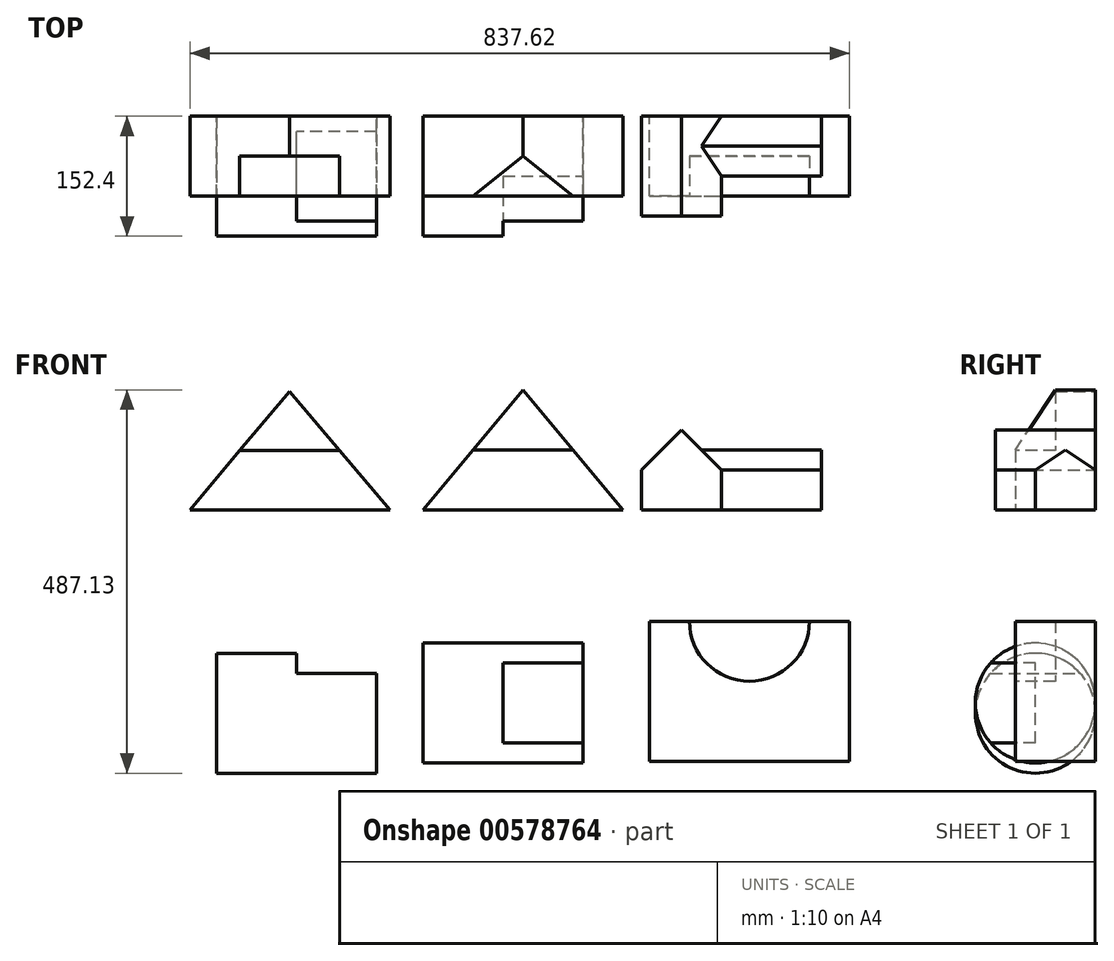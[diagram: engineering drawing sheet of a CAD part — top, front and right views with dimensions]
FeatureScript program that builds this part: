
annotation { "Feature Type Name" : "Feature", "Feature Type Description" : "" }
export const myFeature = defineFeature(function(context is Context, id is Id, definition is map)
    precondition{}
    {
        {
            var Q0;
            Q0=qCreatedBy(makeId("Front.planeOp"),FACE);
            var sketch = newSketch(context, id + "F0", { "sketchPlane" : qUnion([Q0])});
            skLineSegment(sketch, "E0", {"start": v(0, 0) * mm, "end": v(-254, 0) * mm});
            skLineSegment(sketch, "E1", {"start": v(-254, 0) * mm, "end": v(-127, 0) * mm});
            skLineSegment(sketch, "E2", {"start": v(-127.85, 149.9) * mm, "end": v(-254, 0) * mm});
            skLineSegment(sketch, "E3", {"start": v(-127.85, 149.9) * mm, "end": v(0, 0) * mm});
            skLineSegment(sketch, "E4", {"start": v(-127, 76.2) * mm, "end": v(-190.92, 76.2) * mm});
            skPoint(sketch, "E4.endSnap0", {"position": v(-190.92, 74.95) * mm});
            skLineSegment(sketch, "E5", {"start": v(-127, 76.2) * mm, "end": v(-65, 76.2) * mm});
            skLineSegment(sketch, "E6", {"start": v(-127, 0) * mm, "end": v(-127, 76.2) * mm});
            skSolve(sketch);
        }
        {
            var Q0;
            {var subQ0=sQuery(id+"F0.wireOp",EDGE,"E1");Q0=makeQuery(id+"F0.imprint","IMPRINT",FACE,{"disambiguationData":[TD([[makeQuery(id+"F0.imprint","IMPRINT",EDGE,{"derivedFrom":subQ0}),1.0]])]});}
            var Q1;
            {var subQ0=sQuery(id+"F0.wireOp",EDGE,"E0");Q1=makeQuery(id+"F0.imprint","IMPRINT",FACE,{"disambiguationData":[TD([[makeQuery(id+"F0.imprint","IMPRINT",EDGE,{"derivedFrom":subQ0}),-1.0]])]});}
            var Q2;
            {var subQ5=sQuery(id+"F0.wireOp",EDGE,"E5");Q2=makeQuery(id+"F0.imprint","IMPRINT",FACE,{"disambiguationData":[TD([[makeQuery(id+"F0.imprint","IMPRINT",EDGE,{"derivedFrom":subQ5}),1.0]])]});}
            extrude(context, id + "F1", {"entities" : qUnion([Q0, Q1, Q2]), "depth" : 101.6 * mm, "offsetDistance" : 25.4 * mm});
        }
        {
            var Q0;
            Q0=makeQuery(id+"F1.opExtrude","CAP_FACE",FACE,{"disambiguationData":[OSD([sQuery(id+"F0.wireOp",EDGE,"E0"),sQuery(id+"F0.wireOp",EDGE,"E1"),sQuery(id+"F0.wireOp",EDGE,"E2"),sQuery(id+"F0.wireOp",EDGE,"E3")])],"isStart":false});
            var sketch = newSketch(context, id + "F2", { "sketchPlane" : qUnion([Q0])});
            skLineSegment(sketch, "E7", {"start": v(-127, 74.95) * mm, "end": v(-63.92, 74.95) * mm});
            skPoint(sketch, "E7.startSnap0", {"position": v(-127, 0) * mm});
            skPoint(sketch, "E7.startSnap1", {"position": v(-127.85, 74.95) * mm});
            skLineSegment(sketch, "E8", {"start": v(-127, 74.95) * mm, "end": v(-190.92, 74.95) * mm});
            skSolve(sketch);
        }
        {
            var Q0;
            {var subQ0=sQuery(id+"F2.wireOp",EDGE,"E7");Q0=makeQuery(id+"F2.imprint","IMPRINT",FACE,{"disambiguationData":[TD([[makeQuery(id+"F2.imprint","IMPRINT",EDGE,{"derivedFrom":subQ0}),1.0]])]});}
            extrude(context, id + "F3", {"entities" : qUnion([Q0]), "operationType" : NewBodyOperationType.REMOVE, "oppositeDirection" : true, "depth" : 50.8 * mm, "offsetDistance" : 25.4 * mm});
        }
        {
            var Q0;
            Q0=qCreatedBy(makeId("Front.planeOp"),FACE);
            var sketch = newSketch(context, id + "F4", { "sketchPlane" : qUnion([Q0])});
            skLineSegment(sketch, "E9", {"start": v(42.1, 0) * mm, "end": v(296.1, 0) * mm});
            skLineSegment(sketch, "E10", {"start": v(169.1, 152.4) * mm, "end": v(42.1, 0) * mm});
            skLineSegment(sketch, "E11", {"start": v(169.1, 152.4) * mm, "end": v(296.1, 0) * mm});
            skLineSegment(sketch, "E12", {"start": v(169.1, 76.2) * mm, "end": v(105.6, 76.2) * mm});
            skLineSegment(sketch, "E13", {"start": v(169.1, 76.2) * mm, "end": v(232.6, 76.2) * mm});
            skSolve(sketch);
        }
        {
            var Q0;
            {var subQ1=sQuery(id+"F4.wireOp",EDGE,"E9");Q0=makeQuery(id+"F4.imprint","IMPRINT",FACE,{"disambiguationData":[TD([[makeQuery(id+"F4.imprint","IMPRINT",EDGE,{"derivedFrom":subQ1}),1.0]])]});}
            var Q1;
            {var subQ3=sQuery(id+"F4.wireOp",EDGE,"E12");Q1=makeQuery(id+"F4.imprint","IMPRINT",FACE,{"disambiguationData":[TD([[makeQuery(id+"F4.imprint","IMPRINT",EDGE,{"derivedFrom":subQ3}),-1.0]])]});}
            extrude(context, id + "F5", {"entities" : qUnion([Q0, Q1]), "depth" : 101.6 * mm, "offsetDistance" : 25.4 * mm});
        }
        {
            var Q0;
            Q0=makeQuery(id+"F5.opExtrude","CAP_EDGE",EDGE,{"disambiguationData":[OSD([sQuery(id+"F4.wireOp",EDGE,"E9")])],"isStart":false});
            cPoint(context, id + "F6", {"entities" : qUnion([Q0]), "parameter" : 0.5});
        }
        {
            var Q0;
            Q0=makeQuery(id+"F5.opExtrude","CAP_VERTEX",VERTEX,{"disambiguationData":[OSD([sQuery(id+"F4.wireOp",EDGE,"E10"),sQuery(id+"F4.wireOp",EDGE,"E11")])],"isStart":true});
            var Q1;
            Q1=makeQuery(id+"F5.opExtrude","CAP_VERTEX",VERTEX,{"disambiguationData":[OSD([sQuery(id+"F4.wireOp",EDGE,"E10"),sQuery(id+"F4.wireOp",EDGE,"E11")])],"isStart":false});
            var Q2;
            Q2 = qCreatedBy(id + "F6" ,VERTEX);
            cPlane(context, id + "F7", {"entities" : qUnion([Q0, Q1, Q2]), "cplaneType" : CPlaneType.THREE_POINT, "offset" : 25.4 * mm, "width" : 152.4 * mm, "height" : 152.4 * mm});
        }
        {
            var Q0;
            Q0=qCreatedBy(id+"F7.planeOp",FACE);
            var sketch = newSketch(context, id + "F8", { "sketchPlane" : qUnion([Q0])});
            skLineSegment(sketch, "E14", {"start": v(101.6, 76.2) * mm, "end": v(50.8, 152.4) * mm});
            skLineSegment(sketch, "E15", {"start": v(50.8, 152.4) * mm, "end": v(101.6, 152.4) * mm});
            skLineSegment(sketch, "E16", {"start": v(101.6, 152.4) * mm, "end": v(101.6, 76.2) * mm});
            skSolve(sketch);
        }
        {
            var Q0;
            Q0 = qSketchRegion(id + "F8", true);
            extrude(context, id + "F9", {"entities" : qUnion([Q0]), "operationType" : NewBodyOperationType.REMOVE, "endBound" : BoundingType.SYMMETRIC, "depth" : 157.48 * mm, "offsetDistance" : 25.4 * mm});
        }
        {
            var Q0;
            Q0=qCreatedBy(makeId("Front.planeOp"),FACE);
            var sketch = newSketch(context, id + "F10", { "sketchPlane" : qUnion([Q0])});
            skLineSegment(sketch, "E17.bottom", {"start": v(319.7, 0) * mm, "end": v(421.3, 0) * mm});
            skLineSegment(sketch, "E18", {"start": v(370.5, 101.6) * mm, "end": v(319.7, 50.8) * mm});
            skLineSegment(sketch, "E19", {"start": v(370.5, 101.6) * mm, "end": v(421.3, 50.8) * mm});
            skLineSegment(sketch, "E20", {"start": v(319.7, 50.8) * mm, "end": v(319.7, 0) * mm});
            skLineSegment(sketch, "E21", {"start": v(421.3, 0) * mm, "end": v(421.3, 50.8) * mm});
            skSolve(sketch);
        }
        {
            var Q0;
            Q0=makeQuery(id+"F10.imprint","IMPRINT",FACE,{"disambiguationData":[TD([[makeQuery(id+"F10.imprint","IMPRINT",EDGE,{"derivedFrom":sQuery(id+"F10.wireOp",EDGE,"E17.bottom")}),1.0]])]});
            extrude(context, id + "F11", {"entities" : qUnion([Q0]), "depth" : 127 * mm, "offsetDistance" : 25.4 * mm});
        }
        {
            var Q0;
            Q0=makeQuery(id+"F11.opExtrude","CAP_EDGE",EDGE,{"disambiguationData":[OSD([sQuery(id+"F10.wireOp",EDGE,"E17.bottom")])],"isStart":false});
            cPoint(context, id + "F12", {"entities" : qUnion([Q0]), "parameter" : 0.5});
        }
        {
            var Q0;
            Q0=makeQuery(id+"F11.opExtrude","CAP_VERTEX",VERTEX,{"disambiguationData":[OSD([sQuery(id+"F10.wireOp",EDGE,"E18"),sQuery(id+"F10.wireOp",EDGE,"E19")])],"isStart":true});
            var Q1;
            Q1=makeQuery(id+"F11.opExtrude","CAP_VERTEX",VERTEX,{"disambiguationData":[OSD([sQuery(id+"F10.wireOp",EDGE,"E18"),sQuery(id+"F10.wireOp",EDGE,"E19")])],"isStart":false});
            var Q2;
            Q2 = qCreatedBy(id + "F12" ,VERTEX);
            cPlane(context, id + "F13", {"entities" : qUnion([Q0, Q1, Q2]), "cplaneType" : CPlaneType.THREE_POINT, "offset" : 25.4 * mm, "width" : 152.4 * mm, "height" : 152.4 * mm});
        }
        {
            var Q0;
            Q0=qCreatedBy(id+"F13.planeOp",FACE);
            var sketch = newSketch(context, id + "F14", { "sketchPlane" : qUnion([Q0])});
            skLineSegment(sketch, "E22", {"start": v(0, 0) * mm, "end": v(76.2, 0) * mm});
            skLineSegment(sketch, "E23", {"start": v(76.2, 0) * mm, "end": v(76.2, 50.8) * mm});
            skLineSegment(sketch, "E24", {"start": v(0, 50.8) * mm, "end": v(0, 0) * mm});
            skLineSegment(sketch, "E25", {"start": v(76.2, 0) * mm, "end": v(0, 0) * mm});
            skPoint(sketch, "E26.endSnap0", {"position": v(38.1, 0) * mm});
            skLineSegment(sketch, "E27", {"start": v(38.1, 76.2) * mm, "end": v(76.2, 50.8) * mm});
            skLineSegment(sketch, "E28", {"start": v(38.1, 76.2) * mm, "end": v(0, 50.8) * mm});
            skSolve(sketch);
        }
        {
            var Q0;
            Q0=makeQuery(id+"F14.imprint","IMPRINT",FACE,{"disambiguationData":[TD([[makeQuery(id+"F14.imprint","IMPRINT",EDGE,{"derivedFrom":sQuery(id+"F14.wireOp",EDGE,"E23")}),1.0]])]});
            extrude(context, id + "F15", {"entities" : qUnion([Q0]), "operationType" : NewBodyOperationType.ADD, "oppositeDirection" : true, "depth" : 177.8 * mm, "offsetDistance" : 25.4 * mm});
        }
        {
            var Q0;
            Q0=qCreatedBy(makeId("Front.planeOp"),FACE);
            var sketch = newSketch(context, id + "F16", { "sketchPlane" : qUnion([Q0])});
            skLineSegment(sketch, "E29", {"start": v(-220.5, -182.33) * mm, "end": v(-220.5, -334.73) * mm});
            skLineSegment(sketch, "E30", {"start": v(-220.5, -334.73) * mm, "end": v(-17.3, -334.73) * mm});
            skLineSegment(sketch, "E31", {"start": v(-17.3, -334.73) * mm, "end": v(-17.3, -207.73) * mm});
            skLineSegment(sketch, "E32", {"start": v(-17.3, -207.73) * mm, "end": v(-118.9, -207.73) * mm});
            skLineSegment(sketch, "E33", {"start": v(-118.9, -207.73) * mm, "end": v(-118.9, -182.33) * mm});
            skLineSegment(sketch, "E34", {"start": v(-118.9, -182.33) * mm, "end": v(-220.5, -182.33) * mm});
            skSolve(sketch);
        }
        {
            var Q0;
            Q0=makeQuery(id+"F16.imprint","IMPRINT",FACE,{"disambiguationData":[TD([[makeQuery(id+"F16.imprint","IMPRINT",EDGE,{"derivedFrom":sQuery(id+"F16.wireOp",EDGE,"E29")}),1.0]])]});
            extrude(context, id + "F17", {"entities" : qUnion([Q0]), "depth" : 152.4 * mm, "offsetDistance" : 25.4 * mm});
        }
        {
            var Q0;
            Q0=makeQuery(id+"F17.opExtrude","SWEPT_FACE",FACE,{"disambiguationData":[OSD([sQuery(id+"F16.wireOp",EDGE,"E29")])]});
            var sketch = newSketch(context, id + "F18", { "sketchPlane" : qUnion([Q0])});
            skCircle(sketch, "E35", {"center": v(76.2, -258.53) * mm, "radius": 76.2 * mm});
            skSolve(sketch);
        }
        {
            var Q0;
            {var subQ0=sQuery(id+"F18.wireOp",EDGE,"E35");var subQ1=sQuery(id+"F16.wireOp",EDGE,"E29");var subQ4=makeQuery(id+"F17.opExtrude","CAP_EDGE",EDGE,{"disambiguationData":[OSD([subQ1])],"isStart":false});var subQ5=makeQuery(id+"F18.imprint","INTERSECT",VERTEX,{"derivedFrom":[subQ4,subQ0]});Q0=makeQuery(id+"F18.imprint","IMPRINT",FACE,{"disambiguationData":[TD([[makeQuery(id+"F18.imprint","IMPRINT",EDGE,{"disambiguationData":[TD([[subQ5,-1.0]])],"derivedFrom":subQ0}),-1.0]])]});}
            var Q1;
            {var subQ0=sQuery(id+"F18.wireOp",EDGE,"E35");var subQ1=sQuery(id+"F16.wireOp",EDGE,"E29");var subQ2=makeQuery(id+"F17.opExtrude","CAP_EDGE",EDGE,{"disambiguationData":[OSD([subQ1])],"isStart":false});var subQ3=makeQuery(id+"F18.imprint","INTERSECT",VERTEX,{"derivedFrom":[subQ2,subQ0]});Q1=makeQuery(id+"F18.imprint","IMPRINT",FACE,{"disambiguationData":[TD([[makeQuery(id+"F18.imprint","IMPRINT",EDGE,{"disambiguationData":[TD([[subQ3,1.0]])],"derivedFrom":subQ0}),-1.0]])]});}
            var Q2;
            {var subQ0=sQuery(id+"F18.wireOp",EDGE,"E35");var subQ1=sQuery(id+"F16.wireOp",EDGE,"E29");var subQ2=makeQuery(id+"F17.opExtrude","CAP_EDGE",EDGE,{"disambiguationData":[OSD([subQ1])],"isStart":true});var subQ3=makeQuery(id+"F18.imprint","INTERSECT",VERTEX,{"derivedFrom":[subQ2,subQ0]});Q2=makeQuery(id+"F18.imprint","IMPRINT",FACE,{"disambiguationData":[TD([[makeQuery(id+"F18.imprint","IMPRINT",EDGE,{"disambiguationData":[TD([[subQ3,-1.0]])],"derivedFrom":subQ0}),-1.0]])]});}
            var Q3;
            {var subQ0=sQuery(id+"F18.wireOp",EDGE,"E35");var subQ1=sQuery(id+"F16.wireOp",EDGE,"E29");var subQ4=makeQuery(id+"F17.opExtrude","CAP_EDGE",EDGE,{"disambiguationData":[OSD([subQ1])],"isStart":true});var subQ5=makeQuery(id+"F18.imprint","INTERSECT",VERTEX,{"derivedFrom":[subQ4,subQ0]});Q3=makeQuery(id+"F18.imprint","IMPRINT",FACE,{"disambiguationData":[TD([[makeQuery(id+"F18.imprint","IMPRINT",EDGE,{"disambiguationData":[TD([[subQ5,1.0]])],"derivedFrom":subQ0}),-1.0]])]});}
            extrude(context, id + "F19", {"entities" : qUnion([Q0, Q1, Q2, Q3]), "operationType" : NewBodyOperationType.REMOVE, "oppositeDirection" : true, "depth" : 239.78 * mm, "offsetDistance" : 25.4 * mm});
        }
        {
            var Q0;
            Q0=qCreatedBy(makeId("Front.planeOp"),FACE);
            var sketch = newSketch(context, id + "F20", { "sketchPlane" : qUnion([Q0])});
            skLineSegment(sketch, "E36", {"start": v(42.18, -321.7) * mm, "end": v(245.38, -321.7) * mm});
            skLineSegment(sketch, "E37", {"start": v(245.38, -321.7) * mm, "end": v(245.38, -169.3) * mm});
            skLineSegment(sketch, "E38", {"start": v(245.38, -169.3) * mm, "end": v(42.18, -169.3) * mm});
            skLineSegment(sketch, "E39", {"start": v(42.18, -169.3) * mm, "end": v(42.18, -321.7) * mm});
            skLineSegment(sketch, "E40", {"start": v(245.38, -321.7) * mm, "end": v(245.38, -296.3) * mm});
            skLineSegment(sketch, "E41", {"start": v(245.38, -296.3) * mm, "end": v(143.78, -296.3) * mm});
            skLineSegment(sketch, "E42", {"start": v(143.78, -296.3) * mm, "end": v(143.78, -194.7) * mm});
            skLineSegment(sketch, "E43", {"start": v(143.78, -194.7) * mm, "end": v(245.38, -194.7) * mm});
            skSolve(sketch);
        }
        {
            var Q0;
            Q0=makeQuery(id+"F20.imprint","IMPRINT",FACE,{"disambiguationData":[TD([[makeQuery(id+"F20.imprint","IMPRINT",EDGE,{"derivedFrom":sQuery(id+"F20.wireOp",EDGE,"E36")}),1.0]])]});
            var Q1;
            {var subQ0=sQuery(id+"F20.wireOp",EDGE,"E41");Q1=makeQuery(id+"F20.imprint","IMPRINT",FACE,{"disambiguationData":[TD([[makeQuery(id+"F20.imprint","IMPRINT",EDGE,{"derivedFrom":subQ0}),-1.0]])]});}
            extrude(context, id + "F21", {"entities" : qUnion([Q0, Q1]), "depth" : 152.4 * mm, "offsetDistance" : 25.4 * mm});
        }
        {
            var Q0;
            Q0=makeQuery(id+"F21.opExtrude","CAP_FACE",FACE,{"disambiguationData":[OSD([sQuery(id+"F20.wireOp",EDGE,"E36"),sQuery(id+"F20.wireOp",EDGE,"E37"),sQuery(id+"F20.wireOp",EDGE,"E38"),sQuery(id+"F20.wireOp",EDGE,"E39"),sQuery(id+"F20.wireOp",EDGE,"E40")])],"isStart":false});
            var sketch = newSketch(context, id + "F22", { "sketchPlane" : qUnion([Q0])});
            skLineSegment(sketch, "E44", {"start": v(245.38, -321.7) * mm, "end": v(245.38, -296.3) * mm});
            skLineSegment(sketch, "E45", {"start": v(245.38, -296.3) * mm, "end": v(143.78, -296.3) * mm});
            skLineSegment(sketch, "E46", {"start": v(143.78, -296.3) * mm, "end": v(143.78, -194.7) * mm});
            skLineSegment(sketch, "E47", {"start": v(143.78, -194.7) * mm, "end": v(245.38, -194.7) * mm});
            skSolve(sketch);
        }
        {
            var Q0;
            {var subQ0=sQuery(id+"F22.wireOp",EDGE,"E45");Q0=makeQuery(id+"F22.imprint","IMPRINT",FACE,{"disambiguationData":[TD([[makeQuery(id+"F22.imprint","IMPRINT",EDGE,{"derivedFrom":subQ0}),-1.0]])]});}
            extrude(context, id + "F23", {"entities" : qUnion([Q0]), "operationType" : NewBodyOperationType.REMOVE, "oppositeDirection" : true, "depth" : 76.2 * mm, "offsetDistance" : 25.4 * mm});
        }
        {
            var Q0;
            Q0=makeQuery(id+"F21.opExtrude","SWEPT_FACE",FACE,{"disambiguationData":[OSD([sQuery(id+"F20.wireOp",EDGE,"E39")])]});
            var sketch = newSketch(context, id + "F24", { "sketchPlane" : qUnion([Q0])});
            skCircle(sketch, "E48", {"center": v(76.2, -245.5) * mm, "radius": 76.2 * mm});
            skSolve(sketch);
        }
        {
            var Q0;
            {var subQ0=sQuery(id+"F24.wireOp",EDGE,"E48");var subQ1=sQuery(id+"F20.wireOp",EDGE,"E39");var subQ4=makeQuery(id+"F21.opExtrude","CAP_EDGE",EDGE,{"disambiguationData":[OSD([subQ1])],"isStart":false});var subQ5=makeQuery(id+"F24.imprint","INTERSECT",VERTEX,{"derivedFrom":[subQ4,subQ0]});Q0=makeQuery(id+"F24.imprint","IMPRINT",FACE,{"disambiguationData":[TD([[makeQuery(id+"F24.imprint","IMPRINT",EDGE,{"disambiguationData":[TD([[subQ5,-1.0]])],"derivedFrom":subQ0}),-1.0]])]});}
            var Q1;
            {var subQ0=sQuery(id+"F24.wireOp",EDGE,"E48");var subQ1=sQuery(id+"F20.wireOp",EDGE,"E39");var subQ4=makeQuery(id+"F21.opExtrude","CAP_EDGE",EDGE,{"disambiguationData":[OSD([subQ1])],"isStart":true});var subQ5=makeQuery(id+"F24.imprint","INTERSECT",VERTEX,{"derivedFrom":[subQ4,subQ0]});Q1=makeQuery(id+"F24.imprint","IMPRINT",FACE,{"disambiguationData":[TD([[makeQuery(id+"F24.imprint","IMPRINT",EDGE,{"disambiguationData":[TD([[subQ5,1.0]])],"derivedFrom":subQ0}),-1.0]])]});}
            var Q2;
            {var subQ0=sQuery(id+"F24.wireOp",EDGE,"E48");var subQ1=sQuery(id+"F20.wireOp",EDGE,"E39");var subQ2=makeQuery(id+"F21.opExtrude","CAP_EDGE",EDGE,{"disambiguationData":[OSD([subQ1])],"isStart":false});var subQ3=makeQuery(id+"F24.imprint","INTERSECT",VERTEX,{"derivedFrom":[subQ2,subQ0]});Q2=makeQuery(id+"F24.imprint","IMPRINT",FACE,{"disambiguationData":[TD([[makeQuery(id+"F24.imprint","IMPRINT",EDGE,{"disambiguationData":[TD([[subQ3,1.0]])],"derivedFrom":subQ0}),-1.0]])]});}
            var Q3;
            {var subQ0=sQuery(id+"F24.wireOp",EDGE,"E48");var subQ1=sQuery(id+"F20.wireOp",EDGE,"E39");var subQ2=makeQuery(id+"F21.opExtrude","CAP_EDGE",EDGE,{"disambiguationData":[OSD([subQ1])],"isStart":true});var subQ3=makeQuery(id+"F24.imprint","INTERSECT",VERTEX,{"derivedFrom":[subQ2,subQ0]});Q3=makeQuery(id+"F24.imprint","IMPRINT",FACE,{"disambiguationData":[TD([[makeQuery(id+"F24.imprint","IMPRINT",EDGE,{"disambiguationData":[TD([[subQ3,-1.0]])],"derivedFrom":subQ0}),-1.0]])]});}
            extrude(context, id + "F25", {"entities" : qUnion([Q0, Q1, Q2, Q3]), "operationType" : NewBodyOperationType.REMOVE, "oppositeDirection" : true, "depth" : 344.17 * mm, "offsetDistance" : 25.4 * mm});
        }
        {
            var Q0;
            Q0=qCreatedBy(makeId("Front.planeOp"),FACE);
            var sketch = newSketch(context, id + "F26", { "sketchPlane" : qUnion([Q0])});
            skLineSegment(sketch, "E49", {"start": v(329.62, -319.42) * mm, "end": v(583.62, -319.42) * mm});
            skLineSegment(sketch, "E50", {"start": v(583.62, -319.42) * mm, "end": v(583.62, -141.62) * mm});
            skLineSegment(sketch, "E51", {"start": v(583.62, -141.62) * mm, "end": v(329.62, -141.62) * mm});
            skLineSegment(sketch, "E52", {"start": v(329.62, -141.62) * mm, "end": v(329.62, -319.42) * mm});
            skSolve(sketch);
        }
        {
            var Q0;
            Q0=makeQuery(id+"F26.imprint","IMPRINT",FACE,{"disambiguationData":[TD([[makeQuery(id+"F26.imprint","IMPRINT",EDGE,{"derivedFrom":sQuery(id+"F26.wireOp",EDGE,"E49")}),1.0]])]});
            extrude(context, id + "F27", {"entities" : qUnion([Q0]), "depth" : 101.6 * mm, "offsetDistance" : 25.4 * mm});
        }
        {
            var Q0;
            Q0=makeQuery(id+"F27.opExtrude","CAP_FACE",FACE,{"disambiguationData":[OSD([sQuery(id+"F26.wireOp",EDGE,"E49"),sQuery(id+"F26.wireOp",EDGE,"E50"),sQuery(id+"F26.wireOp",EDGE,"E51"),sQuery(id+"F26.wireOp",EDGE,"E52")])],"isStart":false});
            var sketch = newSketch(context, id + "F28", { "sketchPlane" : qUnion([Q0])});
            skCircle(sketch, "E53", {"center": v(456.62, -141.62) * mm, "radius": 76.2 * mm});
            skSolve(sketch);
        }
        {
            var Q0;
            {var subQ0=sQuery(id+"F28.wireOp",EDGE,"E53");var subQ1=makeQuery(id+"F27.opExtrude","CAP_EDGE",EDGE,{"disambiguationData":[OSD([sQuery(id+"F26.wireOp",EDGE,"E51")])],"isStart":false});var subQ2=makeQuery(id+"F28.imprint","INTERSECT",VERTEX,{"disambiguationData":[OD(0.0)],"derivedFrom":[subQ1,subQ0]});Q0=makeQuery(id+"F28.imprint","IMPRINT",FACE,{"disambiguationData":[TD([[makeQuery(id+"F28.imprint","IMPRINT",EDGE,{"disambiguationData":[TD([[subQ2,1.0]])],"derivedFrom":subQ0}),1.0]])]});}
            extrude(context, id + "F29", {"entities" : qUnion([Q0]), "operationType" : NewBodyOperationType.REMOVE, "oppositeDirection" : true, "depth" : 50.8 * mm, "offsetDistance" : 25.4 * mm});
        }
    });
